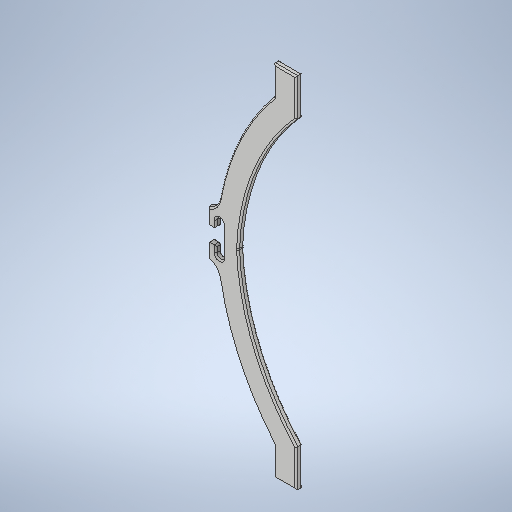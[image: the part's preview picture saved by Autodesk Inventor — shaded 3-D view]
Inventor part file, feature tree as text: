
AUTODESK INVENTOR PART (.ipt)
format: ipt  version: 2025 (Build 290162000, 162)  size: 1,026,048 bytes
history: native  units: mm
features: extrude x3, fillet x2, mirror x1, sketch x1
ambient origin geometry x8: Origin, YZ Plane, XZ Plane, XY Plane, X Axis, Y Axis, Z Axis, Center Point
bodies: Volumenkörper1 (feature_tree)
feature tree (7):
  extrude  "Extrusion1"  Depth=15.0mm
  mirror  "Spiegeln1"
  extrude  "Extrusion2"  Depth=54.0mm
  fillet  "Rundung1"  [1 undecoded]
  fillet  "Rundung2"  Radius=120.0mm
  extrude  "Extrusion3"  Depth=150.0mm
  sketch  "Skizze3"  dims[d0=25.0mm d2=15.0mm d4=54.0mm d5=0.0mm d6=120.0mm d7=150.0mm d9=5.0mm d10=15.0mm d11=15.0mm d12=4.0mm d13=0.0mm d15=10.0mm d16=5.0mm d17=10.0mm d18=5.0mm d19=5.0mm d20=24.0mm d21=4.5mm d22=4.0mm d23=0.0mm d24=10.0mm d25=1.0mm d26=1.0mm d27=0.0mm]
note: 1 required parameter value undecoded (feature->parameter linkage not recoverable at this tier; creation-order binding heuristic only, values carry confidence <= 0.55)
